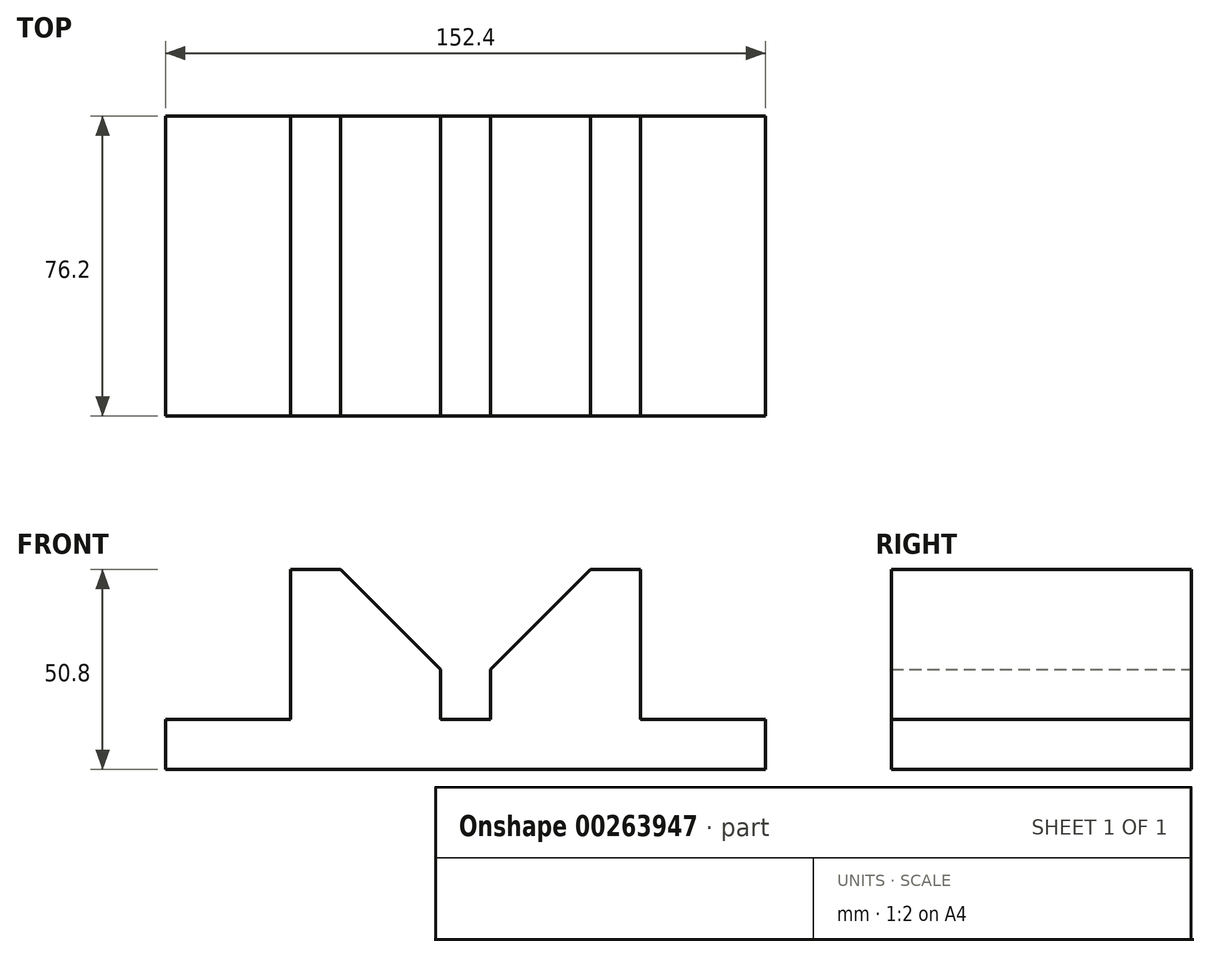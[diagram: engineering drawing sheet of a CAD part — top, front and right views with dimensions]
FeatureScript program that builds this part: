
annotation { "Feature Type Name" : "Feature", "Feature Type Description" : "" }
export const myFeature = defineFeature(function(context is Context, id is Id, definition is map)
    precondition{}
    {
        {
            var Q0;
            Q0=qCreatedBy(makeId("Front.planeOp"),FACE);
            var sketch = newSketch(context, id + "F0", { "sketchPlane" : qUnion([Q0])});
            skLineSegment(sketch, "E0", {"start": v(-76.84, 0) * mm, "end": v(-76.84, 12.7) * mm});
            skLineSegment(sketch, "E1", {"start": v(-76.84, 12.7) * mm, "end": v(-45.1, 12.7) * mm});
            skLineSegment(sketch, "E2", {"start": v(-45.1, 12.7) * mm, "end": v(-45.1, 50.8) * mm});
            skLineSegment(sketch, "E3", {"start": v(-45.1, 50.8) * mm, "end": v(-32.4, 50.8) * mm});
            skLineSegment(sketch, "E4", {"start": v(-32.4, 50.8) * mm, "end": v(-7, 50.8) * mm, "construction": true});
            skLineSegment(sketch, "E5", {"start": v(-7, 50.8) * mm, "end": v(-7, 25.4) * mm, "construction": true});
            skLineSegment(sketch, "E6", {"start": v(-7, 25.4) * mm, "end": v(-32.4, 50.8) * mm});
            skLineSegment(sketch, "E7", {"start": v(-7, 25.4) * mm, "end": v(-7, 12.7) * mm});
            skLineSegment(sketch, "E8", {"start": v(-7, 12.7) * mm, "end": v(5.7, 12.7) * mm});
            skLineSegment(sketch, "E9", {"start": v(5.7, 12.7) * mm, "end": v(5.7, 25.4) * mm});
            skLineSegment(sketch, "E10", {"start": v(5.7, 25.4) * mm, "end": v(5.7, 50.8) * mm, "construction": true});
            skLineSegment(sketch, "E11", {"start": v(5.7, 50.8) * mm, "end": v(31.1, 50.8) * mm, "construction": true});
            skLineSegment(sketch, "E12", {"start": v(31.1, 50.8) * mm, "end": v(5.7, 25.4) * mm});
            skLineSegment(sketch, "E13", {"start": v(31.1, 50.8) * mm, "end": v(43.8, 50.8) * mm});
            skLineSegment(sketch, "E14", {"start": v(43.8, 50.8) * mm, "end": v(43.8, 12.7) * mm});
            skLineSegment(sketch, "E15", {"start": v(43.8, 12.7) * mm, "end": v(75.56, 12.7) * mm});
            skLineSegment(sketch, "E16", {"start": v(75.56, 12.7) * mm, "end": v(75.56, 0) * mm});
            skLineSegment(sketch, "E17", {"start": v(75.56, 0) * mm, "end": v(-76.84, 0) * mm});
            skSolve(sketch);
        }
        {
            var Q0;
            Q0 = qSketchRegion(id + "F0", true);
            extrude(context, id + "F1", {"entities" : qUnion([Q0]), "depth" : 76.2 * mm});
        }
    });
